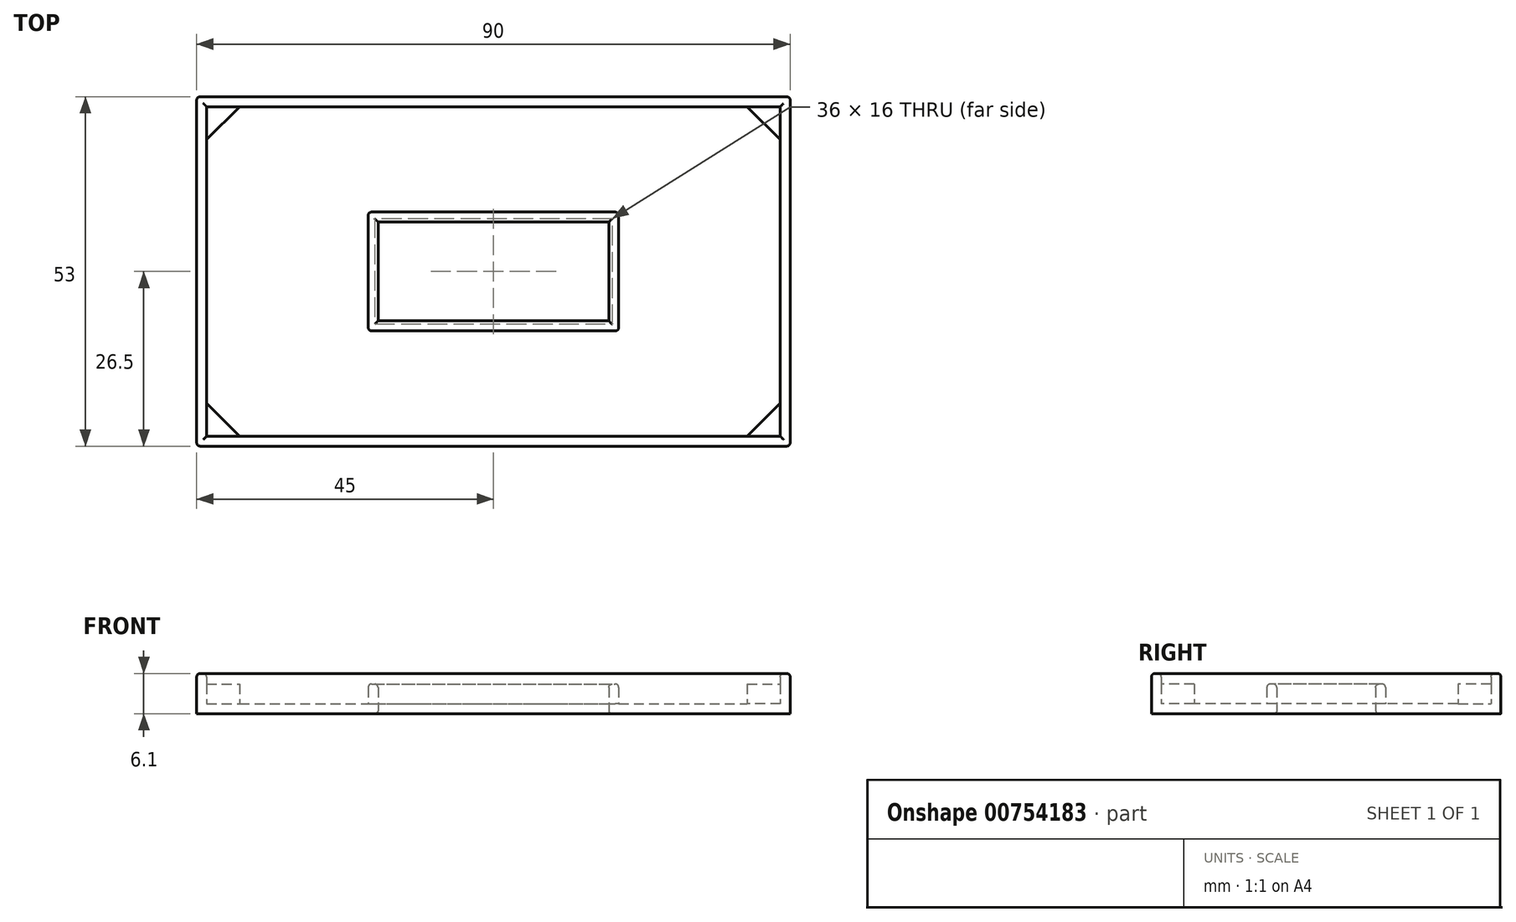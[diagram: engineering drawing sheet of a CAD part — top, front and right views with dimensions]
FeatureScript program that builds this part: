
annotation { "Feature Type Name" : "Feature", "Feature Type Description" : "" }
export const myFeature = defineFeature(function(context is Context, id is Id, definition is map)
    precondition{}
    {
        {
            var Q0;
            Q0=qCreatedBy(makeId("Top.planeOp"),FACE);
            var sketch = newSketch(context, id + "F0", { "sketchPlane" : qUnion([Q0])});
            skLineSegment(sketch, "E0.bottom", {"start": v(-43.5, 25) * mm, "end": v(43.5, 25) * mm});
            skLineSegment(sketch, "E0.top", {"start": v(-43.5, -25) * mm, "end": v(43.5, -25) * mm});
            skLineSegment(sketch, "E0.left", {"start": v(-43.5, 25) * mm, "end": v(-43.5, -25) * mm});
            skLineSegment(sketch, "E0.right", {"start": v(43.5, 25) * mm, "end": v(43.5, -25) * mm});
            skLineSegment(sketch, "E1", {"start": v(0, 25) * mm, "end": v(0, -25) * mm, "construction": true});
            skSolve(sketch);
        }
        {
            var Q0;
            Q0=qCreatedBy(makeId("Top.planeOp"),FACE);
            var sketch = newSketch(context, id + "F1", { "sketchPlane" : qUnion([Q0])});
            skLineSegment(sketch, "E2.0", {"start": v(-43.5, 25) * mm, "end": v(43.5, 25) * mm, "construction": true});
            skLineSegment(sketch, "E2.1", {"start": v(-43.5, 25) * mm, "end": v(-43.5, -25) * mm, "construction": true});
            skLineSegment(sketch, "E2.2", {"start": v(-43.5, -25) * mm, "end": v(43.5, -25) * mm, "construction": true});
            skLineSegment(sketch, "E2.3", {"start": v(43.5, 25) * mm, "end": v(43.5, -25) * mm, "construction": true});
            skLineSegment(sketch, "E3.0", {"start": v(-45, 26.5) * mm, "end": v(45, 26.5) * mm});
            skLineSegment(sketch, "E3.1", {"start": v(-45, 26.5) * mm, "end": v(-45, -26.5) * mm});
            skLineSegment(sketch, "E3.2", {"start": v(-45, -26.5) * mm, "end": v(45, -26.5) * mm});
            skLineSegment(sketch, "E3.3", {"start": v(45, 26.5) * mm, "end": v(45, -26.5) * mm});
            skLineSegment(sketch, "E4.bottom", {"start": v(-17.5, 7.5) * mm, "end": v(17.5, 7.5) * mm});
            skLineSegment(sketch, "E4.top", {"start": v(-17.5, -7.5) * mm, "end": v(17.5, -7.5) * mm});
            skLineSegment(sketch, "E4.left", {"start": v(-17.5, 7.5) * mm, "end": v(-17.5, -7.5) * mm});
            skLineSegment(sketch, "E4.right", {"start": v(17.5, 7.5) * mm, "end": v(17.5, -7.5) * mm});
            skLineSegment(sketch, "E5", {"start": v(0, 7.5) * mm, "end": v(0, -7.5) * mm, "construction": true});
            skSolve(sketch);
        }
        {
            var Q0;
            Q0 = qSketchRegion(id + "F1", true);
            extrude(context, id + "F2", {"entities" : qUnion([Q0]), "depth" : 1.5 * mm, "offsetDistance" : 25 * mm});
        }
        {
            var Q0;
            Q0=makeQuery(id+"F2.opExtrude","CAP_FACE",FACE,{"disambiguationData":[OSD([sQuery(id+"F1.wireOp",EDGE,"E3.0"),sQuery(id+"F1.wireOp",EDGE,"E3.1"),sQuery(id+"F1.wireOp",EDGE,"E3.2"),sQuery(id+"F1.wireOp",EDGE,"E3.3"),sQuery(id+"F1.wireOp",EDGE,"E4.bottom"),sQuery(id+"F1.wireOp",EDGE,"E4.top"),sQuery(id+"F1.wireOp",EDGE,"E4.left"),sQuery(id+"F1.wireOp",EDGE,"E4.right")])],"isStart":false});
            var sketch = newSketch(context, id + "F3", { "sketchPlane" : qUnion([Q0])});
            skLineSegment(sketch, "E6.0", {"start": v(-43.5, 25) * mm, "end": v(43.5, 25) * mm});
            skLineSegment(sketch, "E6.1", {"start": v(-43.5, 25) * mm, "end": v(-43.5, -25) * mm});
            skLineSegment(sketch, "E6.2", {"start": v(-43.5, -25) * mm, "end": v(43.5, -25) * mm});
            skLineSegment(sketch, "E6.3", {"start": v(43.5, 25) * mm, "end": v(43.5, -25) * mm});
            skLineSegment(sketch, "E7.0", {"start": v(-45, 26.5) * mm, "end": v(45, 26.5) * mm});
            skLineSegment(sketch, "E7.1", {"start": v(-45, 26.5) * mm, "end": v(-45, -26.5) * mm});
            skLineSegment(sketch, "E7.2", {"start": v(45, 26.5) * mm, "end": v(45, -26.5) * mm});
            skLineSegment(sketch, "E7.3", {"start": v(-45, -26.5) * mm, "end": v(45, -26.5) * mm});
            skSolve(sketch);
        }
        {
            var Q0;
            Q0 = qSketchRegion(id + "F3", true);
            extrude(context, id + "F4", {"entities" : qUnion([Q0]), "operationType" : NewBodyOperationType.ADD, "depth" : 4.6 * mm, "offsetDistance" : 25 * mm});
        }
        {
            var Q0;
            Q0=makeQuery(id+"F2.opExtrude","CAP_FACE",FACE,{"disambiguationData":[OSD([sQuery(id+"F1.wireOp",EDGE,"E3.1"),sQuery(id+"F1.wireOp",EDGE,"E3.3"),sQuery(id+"F1.wireOp",EDGE,"mlNhEq57-cEdN-hlKx-6O5a-k7beKD7LGbqi"),sQuery(id+"F1.wireOp",EDGE,"IyTA8bUb-VmV5-8Eda-VbmE-xSy0DSjlYYFq"),sQuery(id+"F1.wireOp",EDGE,"EL4vXUiF-J6qK-eItM-pItL-jxxmpN3wNXK5"),sQuery(id+"F1.wireOp",EDGE,"32352735-671d-4652-813e-9623be5d1e13.filletArc"),sQuery(id+"F1.wireOp",EDGE,"c133f9ee-6f37-4854-8f29-a4a2d77676eb.filletArc"),sQuery(id+"F1.wireOp",EDGE,"f2b2c9b6-4393-4b0d-8f83-86d509ed28f60.MirrorCS"),sQuery(id+"F1.wireOp",EDGE,"d4c2bd27-4483-48c9-85fa-bc53ea76ffd50.MirrorCS"),sQuery(id+"F1.wireOp",EDGE,"194cfd48-f2cd-46b0-ac90-79163fbc6c670.MirrorCS"),sQuery(id+"F1.wireOp",EDGE,"3f4de770-7133-495a-b4b1-24c9c766f8630.MirrorCS"),sQuery(id+"F1.wireOp",EDGE,"b5a549db-6cb2-412a-b1aa-66bbe92102950.MirrorCS"),sQuery(id+"F1.wireOp",EDGE,"E4.bottom"),sQuery(id+"F1.wireOp",EDGE,"E4.top"),sQuery(id+"F1.wireOp",EDGE,"E4.left"),sQuery(id+"F1.wireOp",EDGE,"E4.right")])],"isStart":false});
            var sketch = newSketch(context, id + "F5", { "sketchPlane" : qUnion([Q0])});
            skLineSegment(sketch, "E8", {"start": v(-43.5, 25) * mm, "end": v(-43.5, 20) * mm});
            skLineSegment(sketch, "E9", {"start": v(-43.5, 20) * mm, "end": v(-38.5, 25) * mm});
            skLineSegment(sketch, "E10", {"start": v(-38.5, 25) * mm, "end": v(-43.5, 25) * mm});
            skLineSegment(sketch, "E11", {"start": v(-43.5, 25) * mm, "end": v(-38.5, 25) * mm});
            skLineSegment(sketch, "E12.MirrorCS", {"start": v(43.5, 25) * mm, "end": v(38.5, 25) * mm});
            skLineSegment(sketch, "E13.MirrorCS", {"start": v(43.5, 25) * mm, "end": v(43.5, 20) * mm});
            skLineSegment(sketch, "E14.MirrorCS", {"start": v(43.5, 20) * mm, "end": v(38.5, 25) * mm});
            skLineSegment(sketch, "E15.MirrorCS", {"start": v(-43.5, -25) * mm, "end": v(-38.5, -25) * mm});
            skLineSegment(sketch, "E16.MirrorCS", {"start": v(-43.5, -25) * mm, "end": v(-43.5, -20) * mm});
            skLineSegment(sketch, "E17.MirrorCS", {"start": v(-43.5, -20) * mm, "end": v(-38.5, -25) * mm});
            skLineSegment(sketch, "E18.MirrorCS", {"start": v(43.5, -25) * mm, "end": v(38.5, -25) * mm});
            skLineSegment(sketch, "E19.MirrorCS", {"start": v(43.5, -25) * mm, "end": v(43.5, -20) * mm});
            skLineSegment(sketch, "E20.MirrorCS", {"start": v(43.5, -20) * mm, "end": v(38.5, -25) * mm});
            skLineSegment(sketch, "E21.0", {"start": v(-17.5, 7.5) * mm, "end": v(17.5, 7.5) * mm});
            skLineSegment(sketch, "E21.1", {"start": v(-17.5, 7.5) * mm, "end": v(-17.5, -7.5) * mm});
            skLineSegment(sketch, "E21.2", {"start": v(-17.5, -7.5) * mm, "end": v(17.5, -7.5) * mm});
            skLineSegment(sketch, "E21.3", {"start": v(17.5, 7.5) * mm, "end": v(17.5, -7.5) * mm});
            skLineSegment(sketch, "E22.0", {"start": v(-19, -9) * mm, "end": v(19, -9) * mm});
            skLineSegment(sketch, "E22.1", {"start": v(-19, 9) * mm, "end": v(-19, -9) * mm});
            skLineSegment(sketch, "E22.2", {"start": v(-19, 9) * mm, "end": v(19, 9) * mm});
            skLineSegment(sketch, "E22.3", {"start": v(19, 9) * mm, "end": v(19, -9) * mm});
            skSolve(sketch);
        }
        {
            var Q0;
            Q0 = qSketchRegion(id + "F5", true);
            extrude(context, id + "F6", {"entities" : qUnion([Q0]), "operationType" : NewBodyOperationType.ADD, "depth" : 3 * mm, "offsetDistance" : 25 * mm});
        }
        {
            var Q0;
            Q0=makeQuery(id+"F4.boolean.opBoolean","MERGE",EDGE,{"derivedFrom":[makeQuery(id+"F2.opExtrude","SWEPT_EDGE",EDGE,{"disambiguationData":[OSD([sQuery(id+"F1.wireOp",EDGE,"E3.1"),sQuery(id+"F1.wireOp",EDGE,"E3.2")])]}),makeQuery(id+"F4.opExtrude","SWEPT_EDGE",EDGE,{"disambiguationData":[OSD([sQuery(id+"F3.wireOp",EDGE,"E7.1"),sQuery(id+"F3.wireOp",EDGE,"E7.3")])]})]});
            var Q1;
            Q1=makeQuery(id+"F4.boolean.opBoolean","MERGE",EDGE,{"derivedFrom":[makeQuery(id+"F2.opExtrude","SWEPT_EDGE",EDGE,{"disambiguationData":[OSD([sQuery(id+"F1.wireOp",EDGE,"E3.2"),sQuery(id+"F1.wireOp",EDGE,"E3.3")])]}),makeQuery(id+"F4.opExtrude","SWEPT_EDGE",EDGE,{"disambiguationData":[OSD([sQuery(id+"F3.wireOp",EDGE,"E7.2"),sQuery(id+"F3.wireOp",EDGE,"E7.3")])]})]});
            var Q2;
            Q2=makeQuery(id+"F4.boolean.opBoolean","MERGE",EDGE,{"derivedFrom":[makeQuery(id+"F2.opExtrude","SWEPT_EDGE",EDGE,{"disambiguationData":[OSD([sQuery(id+"F1.wireOp",EDGE,"E3.0"),sQuery(id+"F1.wireOp",EDGE,"E3.3")])]}),makeQuery(id+"F4.opExtrude","SWEPT_EDGE",EDGE,{"disambiguationData":[OSD([sQuery(id+"F3.wireOp",EDGE,"E7.0"),sQuery(id+"F3.wireOp",EDGE,"E7.2")])]})]});
            var Q3;
            Q3=makeQuery(id+"F4.boolean.opBoolean","MERGE",EDGE,{"derivedFrom":[makeQuery(id+"F2.opExtrude","SWEPT_EDGE",EDGE,{"disambiguationData":[OSD([sQuery(id+"F1.wireOp",EDGE,"E3.0"),sQuery(id+"F1.wireOp",EDGE,"E3.1")])]}),makeQuery(id+"F4.opExtrude","SWEPT_EDGE",EDGE,{"disambiguationData":[OSD([sQuery(id+"F3.wireOp",EDGE,"E7.0"),sQuery(id+"F3.wireOp",EDGE,"E7.1")])]})]});
            var Q4;
            Q4=makeQuery(id+"F4.opExtrude","CAP_EDGE",EDGE,{"disambiguationData":[OSD([sQuery(id+"F3.wireOp",EDGE,"E7.0")])],"isStart":false});
            var Q5;
            Q5=makeQuery(id+"F4.opExtrude","CAP_EDGE",EDGE,{"disambiguationData":[OSD([sQuery(id+"F3.wireOp",EDGE,"E7.1")])],"isStart":false});
            var Q6;
            Q6=makeQuery(id+"F4.opExtrude","CAP_EDGE",EDGE,{"disambiguationData":[OSD([sQuery(id+"F3.wireOp",EDGE,"E7.2")])],"isStart":false});
            var Q7;
            Q7=makeQuery(id+"F4.opExtrude","CAP_EDGE",EDGE,{"disambiguationData":[OSD([sQuery(id+"F3.wireOp",EDGE,"E7.3")])],"isStart":false});
            var Q8;
            Q8=makeQuery(id+"F4.opExtrude","CAP_EDGE",EDGE,{"disambiguationData":[OSD([sQuery(id+"F3.wireOp",EDGE,"E6.1")])],"isStart":false});
            var Q9;
            Q9=makeQuery(id+"F4.opExtrude","CAP_EDGE",EDGE,{"disambiguationData":[OSD([sQuery(id+"F3.wireOp",EDGE,"E6.0")])],"isStart":false});
            var Q10;
            Q10=makeQuery(id+"F4.opExtrude","CAP_EDGE",EDGE,{"disambiguationData":[OSD([sQuery(id+"F3.wireOp",EDGE,"E6.3")])],"isStart":false});
            var Q11;
            Q11=makeQuery(id+"F4.opExtrude","CAP_EDGE",EDGE,{"disambiguationData":[OSD([sQuery(id+"F3.wireOp",EDGE,"E6.2")])],"isStart":false});
            var Q12;
            Q12=makeQuery(id+"F6.opExtrude","CAP_EDGE",EDGE,{"disambiguationData":[OSD([sQuery(id+"F5.wireOp",EDGE,"E22.0")])],"isStart":false});
            var Q13;
            Q13=makeQuery(id+"F6.opExtrude","CAP_EDGE",EDGE,{"disambiguationData":[OSD([sQuery(id+"F5.wireOp",EDGE,"E22.3")])],"isStart":false});
            var Q14;
            Q14=makeQuery(id+"F6.opExtrude","CAP_EDGE",EDGE,{"disambiguationData":[OSD([sQuery(id+"F5.wireOp",EDGE,"E21.0")])],"isStart":false});
            var Q15;
            Q15=makeQuery(id+"F6.opExtrude","CAP_EDGE",EDGE,{"disambiguationData":[OSD([sQuery(id+"F5.wireOp",EDGE,"E22.2")])],"isStart":false});
            var Q16;
            Q16=makeQuery(id+"F6.opExtrude","CAP_EDGE",EDGE,{"disambiguationData":[OSD([sQuery(id+"F5.wireOp",EDGE,"E21.3")])],"isStart":false});
            var Q17;
            Q17=makeQuery(id+"F6.opExtrude","CAP_EDGE",EDGE,{"disambiguationData":[OSD([sQuery(id+"F5.wireOp",EDGE,"E21.1")])],"isStart":false});
            var Q18;
            Q18=makeQuery(id+"F6.opExtrude","CAP_EDGE",EDGE,{"disambiguationData":[OSD([sQuery(id+"F5.wireOp",EDGE,"E22.1")])],"isStart":false});
            var Q19;
            Q19=makeQuery(id+"F2.opExtrude","CAP_EDGE",EDGE,{"disambiguationData":[OSD([sQuery(id+"F1.wireOp",EDGE,"E4.bottom")])],"isStart":true});
            var Q20;
            Q20=makeQuery(id+"F2.opExtrude","CAP_EDGE",EDGE,{"disambiguationData":[OSD([sQuery(id+"F1.wireOp",EDGE,"E4.left")])],"isStart":true});
            var Q21;
            Q21=makeQuery(id+"F2.opExtrude","CAP_EDGE",EDGE,{"disambiguationData":[OSD([sQuery(id+"F1.wireOp",EDGE,"E4.top")])],"isStart":true});
            var Q22;
            Q22=makeQuery(id+"F2.opExtrude","CAP_EDGE",EDGE,{"disambiguationData":[OSD([sQuery(id+"F1.wireOp",EDGE,"E4.right")])],"isStart":true});
            var Q23;
            Q23=makeQuery(id+"F6.opExtrude","SWEPT_EDGE",EDGE,{"disambiguationData":[OSD([sQuery(id+"F5.wireOp",EDGE,"E22.0"),sQuery(id+"F5.wireOp",EDGE,"E22.1")])]});
            var Q24;
            Q24=makeQuery(id+"F6.opExtrude","SWEPT_EDGE",EDGE,{"disambiguationData":[OSD([sQuery(id+"F5.wireOp",EDGE,"E22.1"),sQuery(id+"F5.wireOp",EDGE,"E22.2")])]});
            var Q25;
            Q25=makeQuery(id+"F6.opExtrude","CAP_EDGE",EDGE,{"disambiguationData":[OSD([sQuery(id+"F5.wireOp",EDGE,"E22.1")])],"isStart":true});
            var Q26;
            Q26=makeQuery(id+"F6.opExtrude","CAP_EDGE",EDGE,{"disambiguationData":[OSD([sQuery(id+"F5.wireOp",EDGE,"E21.2")])],"isStart":false});
            var Q27;
            Q27=makeQuery(id+"F6.opExtrude","CAP_EDGE",EDGE,{"disambiguationData":[OSD([sQuery(id+"F5.wireOp",EDGE,"E22.3")])],"isStart":true});
            var Q28;
            Q28=makeQuery(id+"F6.opExtrude","SWEPT_EDGE",EDGE,{"disambiguationData":[OSD([sQuery(id+"F5.wireOp",EDGE,"E22.2"),sQuery(id+"F5.wireOp",EDGE,"E22.3")])]});
            var Q29;
            Q29=makeQuery(id+"F6.opExtrude","SWEPT_EDGE",EDGE,{"disambiguationData":[OSD([sQuery(id+"F5.wireOp",EDGE,"E22.0"),sQuery(id+"F5.wireOp",EDGE,"E22.3")])]});
            var Q30;
            Q30=makeQuery(id+"F4.opExtrude","CAP_EDGE",EDGE,{"disambiguationData":[OSD([sQuery(id+"F3.wireOp",EDGE,"E6.1")])],"isStart":true});
            var Q31;
            Q31=makeQuery(id+"F6.opExtrude","CAP_EDGE",EDGE,{"disambiguationData":[OSD([sQuery(id+"F5.wireOp",EDGE,"E17.MirrorCS")])],"isStart":true});
            var Q32;
            Q32=makeQuery(id+"F6.opExtrude","CAP_EDGE",EDGE,{"disambiguationData":[OSD([sQuery(id+"F5.wireOp",EDGE,"E9")])],"isStart":true});
            var Q33;
            Q33=makeQuery(id+"F4.opExtrude","CAP_EDGE",EDGE,{"disambiguationData":[OSD([sQuery(id+"F3.wireOp",EDGE,"E6.0")])],"isStart":true});
            var Q34;
            Q34=makeQuery(id+"F6.opExtrude","CAP_EDGE",EDGE,{"disambiguationData":[OSD([sQuery(id+"F5.wireOp",EDGE,"E14.MirrorCS")])],"isStart":true});
            var Q35;
            Q35=makeQuery(id+"F4.opExtrude","CAP_EDGE",EDGE,{"disambiguationData":[OSD([sQuery(id+"F3.wireOp",EDGE,"E6.3")])],"isStart":true});
            var Q36;
            Q36=makeQuery(id+"F6.opExtrude","CAP_EDGE",EDGE,{"disambiguationData":[OSD([sQuery(id+"F5.wireOp",EDGE,"E20.MirrorCS")])],"isStart":true});
            var Q37;
            Q37=makeQuery(id+"F4.opExtrude","CAP_EDGE",EDGE,{"disambiguationData":[OSD([sQuery(id+"F3.wireOp",EDGE,"E6.2")])],"isStart":true});
            fillet(context, id + "F7", {"entities" : qUnion([Q0, Q1, Q2, Q3, Q4, Q5, Q6, Q7, Q8, Q9, Q10, Q11, Q12, Q13, Q14, Q15, Q16, Q17, Q18, Q19, Q20, Q21, Q22, Q23, Q24, Q25, Q26, Q27, Q28, Q29, Q30, Q31, Q32, Q33, Q34, Q35, Q36, Q37]), "radius" : 0.5 * mm, "tangentPropagation" : true, "allowEdgeOverflow" : false});
        }
    });
